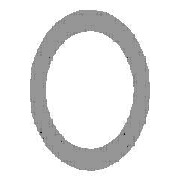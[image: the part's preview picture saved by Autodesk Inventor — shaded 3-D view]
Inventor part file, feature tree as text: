
AUTODESK INVENTOR PART (.ipt)
format: ipt  version: 2013 (Build 170138000, 138)  size: 135,168 bytes
history: native  units: mm (DEFAULTED — no unit token found)
features: plane x6, sketch x6, other x4, extrude x3, reference x1
ambient origin geometry x8: Origin, YZ Plane, XZ Plane, XY Plane, X Axis, Y Axis, Z Axis, Center Point
bodies: Solid1 (feature_tree), Body (feature_tree)
feature tree (20):
  parser-record x1  (decoder bookkeeping rows leaked as tree rows — omitted from the tree; the rows remain in map.json)
  other  "Driven Length"
  other  "Start plane"
  other  "End plane"
  plane  "Work Plane4"
  plane  "Work Plane5"
  plane  "Work Plane6"
  extrude  "Extrusion2"  Depth=3.3782mm
  plane  "Work Plane7"
  extrude  "Extrusion3"  TaperAngle=0.0deg  [1 undecoded]
  plane  "Work Plane8"
  extrude  "Extrusion4"  TaperAngle=90.0deg  [1 undecoded]
  sketch  "Sketch"  dims[d10=25.4mm d11=0.0mm d12=6.35mm d13=25.4mm d14=0.0mm]
  sketch  "Sketch3"  dims[d0=33.401mm d1=3.3782mm]
  plane  "Work Plane3"
  sketch  "Sketch4"  dims[d2=800.1mm d3=0.0mm d4=-0.0mm]
  sketch  "Sketch5"  dims[d5=800.1mm d6=90.0deg]
  sketch  "Sketch6"  dims[d7=800.1mm]
  reference  "Reference1"
  sketch  "Sketch7"  dims[d8=3.302mm d9=0.0mm]
note: 2 required parameter values undecoded (feature->parameter linkage not recoverable at this tier; creation-order binding heuristic only, values carry confidence <= 0.55)
